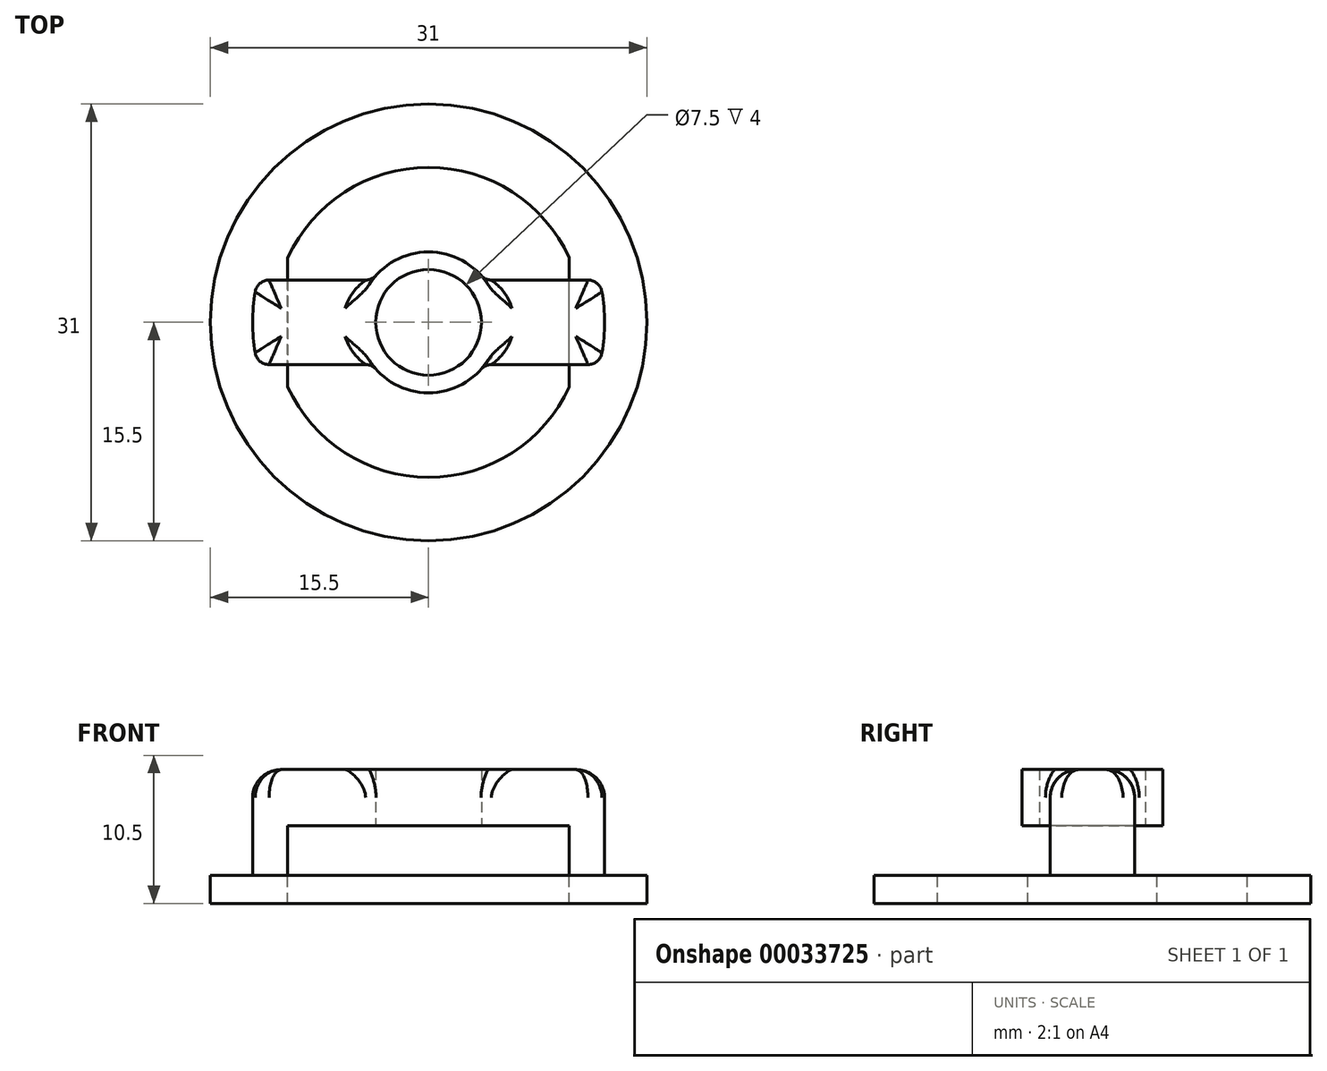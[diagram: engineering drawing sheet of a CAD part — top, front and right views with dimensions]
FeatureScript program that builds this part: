
annotation { "Feature Type Name" : "Feature", "Feature Type Description" : "" }
export const myFeature = defineFeature(function(context is Context, id is Id, definition is map)
    precondition{}
    {
        {
            var Q0;
            Q0=qCreatedBy(makeId("Top.planeOp"),FACE);
            var sketch = newSketch(context, id + "F0", { "sketchPlane" : qUnion([Q0])});
            skCircle(sketch, "E0", {"center": v(0, 0) * mm, "radius": 15.5 * mm});
            skLineSegment(sketch, "E1", {"start": v(-12.13, 3) * mm, "end": v(-10, 3) * mm});
            skLineSegment(sketch, "E2", {"start": v(-12.13, -3) * mm, "end": v(-10, -3) * mm});
            skLineSegment(sketch, "E3", {"start": v(-10, 0) * mm, "end": v(-10, 4.58) * mm});
            skLineSegment(sketch, "E4", {"start": v(-10, 0) * mm, "end": v(-10, -4.58) * mm});
            skLineSegment(sketch, "E5", {"start": v(10, -3) * mm, "end": v(12.13, -3) * mm});
            skLineSegment(sketch, "E6", {"start": v(10, 3) * mm, "end": v(12.13, 3) * mm});
            skLineSegment(sketch, "E7", {"start": v(10, -4.58) * mm, "end": v(10, 4.58) * mm});
            skArc(sketch, "E8", {"start": v(-10, -4.58) * mm, "mid": v(0, -11) * mm, "end": v(10, -4.58) * mm});
            skArc(sketch, "E9", {"start": v(10, 4.58) * mm, "mid": v(0, 11) * mm, "end": v(-10, 4.58) * mm});
            skArc(sketch, "E10", {"start": v(-12.13, 3) * mm, "mid": v(-12.5, 0) * mm, "end": v(-12.13, -3) * mm});
            skArc(sketch, "E11", {"start": v(12.13, -3) * mm, "mid": v(12.5, 0) * mm, "end": v(12.13, 3) * mm});
            skSolve(sketch);
        }
        {
            var Q0;
            Q0=makeQuery(id+"F0.imprint","IMPRINT",FACE,{"disambiguationData":[TD([[makeQuery(id+"F0.imprint","IMPRINT",EDGE,{"derivedFrom":sQuery(id+"F0.wireOp",EDGE,"E0")}),1.0]])]});
            var Q1;
            {var subQ4=sQuery(id+"F0.wireOp",EDGE,"E1");Q1=makeQuery(id+"F0.imprint","IMPRINT",FACE,{"disambiguationData":[TD([[makeQuery(id+"F0.imprint","IMPRINT",EDGE,{"derivedFrom":subQ4}),-1.0]])]});}
            var Q2;
            {var subQ2=sQuery(id+"F0.wireOp",EDGE,"E5");Q2=makeQuery(id+"F0.imprint","IMPRINT",FACE,{"disambiguationData":[TD([[makeQuery(id+"F0.imprint","IMPRINT",EDGE,{"derivedFrom":subQ2}),1.0]])]});}
            extrude(context, id + "F1", {"entities" : qUnion([Q0, Q1, Q2]), "oppositeDirection" : true, "depth" : 2 * mm});
        }
        {
            var Q0;
            {var subQ4=sQuery(id+"F0.wireOp",EDGE,"E1");Q0=makeQuery(id+"F0.imprint","IMPRINT",FACE,{"disambiguationData":[TD([[makeQuery(id+"F0.imprint","IMPRINT",EDGE,{"derivedFrom":subQ4}),-1.0]])]});}
            var Q1;
            {var subQ2=sQuery(id+"F0.wireOp",EDGE,"E5");Q1=makeQuery(id+"F0.imprint","IMPRINT",FACE,{"disambiguationData":[TD([[makeQuery(id+"F0.imprint","IMPRINT",EDGE,{"derivedFrom":subQ2}),1.0]])]});}
            extrude(context, id + "F2", {"entities" : qUnion([Q0, Q1]), "operationType" : NewBodyOperationType.ADD, "depth" : 3.5 * mm});
        }
        {
            var Q0;
            Q0=makeQuery(id+"F2.opExtrude","CAP_FACE",FACE,{"disambiguationData":[OSD([sQuery(id+"F0.wireOp",EDGE,"E1"),sQuery(id+"F0.wireOp",EDGE,"E2"),sQuery(id+"F0.wireOp",EDGE,"E3"),sQuery(id+"F0.wireOp",EDGE,"E4"),sQuery(id+"F0.wireOp",EDGE,"E10")])],"isStart":false});
            var sketch = newSketch(context, id + "F3", { "sketchPlane" : qUnion([Q0])});
            skCircle(sketch, "E12", {"center": v(0, 0) * mm, "radius": 3.75 * mm});
            skCircle(sketch, "E13", {"center": v(0, 0) * mm, "radius": 5 * mm});
            skLineSegment(sketch, "E14", {"start": v(-10, 3) * mm, "end": v(-4, 3) * mm});
            skLineSegment(sketch, "E15", {"start": v(-10, -3) * mm, "end": v(-4, -3) * mm});
            skLineSegment(sketch, "E16.0.0", {"start": v(10, 3) * mm, "end": v(10, -3) * mm});
            skLineSegment(sketch, "E16.0.1", {"start": v(10, -3) * mm, "end": v(12.13, -3) * mm});
            skArc(sketch, "E16.0.2", {"start": v(12.13, -3) * mm, "mid": v(12.5, 0) * mm, "end": v(12.13, 3) * mm});
            skLineSegment(sketch, "E16.0.3", {"start": v(12.13, 3) * mm, "end": v(10, 3) * mm});
            skLineSegment(sketch, "E17", {"start": v(10, 3) * mm, "end": v(4, 3) * mm});
            skLineSegment(sketch, "E18", {"start": v(10, -3) * mm, "end": v(4, -3) * mm});
            skSolve(sketch);
        }
        {
            var Q0;
            Q0 = qSketchRegion(id + "F3", true);
            var Q1;
            {var subQ1=sQuery(id+"F3.wireOp",EDGE,"E14");Q1=makeQuery(id+"F3.imprint","IMPRINT",FACE,{"disambiguationData":[TD([[makeQuery(id+"F3.imprint","IMPRINT",EDGE,{"derivedFrom":subQ1}),-1.0]])]});}
            var Q2;
            Q2=makeQuery(id+"F3.imprint","IMPRINT",FACE,{"disambiguationData":[TD([[makeQuery(id+"F3.imprint","IMPRINT",EDGE,{"derivedFrom":makeQuery(id+"F2.opExtrude","CAP_EDGE",EDGE,{"disambiguationData":[OSD([sQuery(id+"F0.wireOp",EDGE,"E1")])],"isStart":false})}),-1.0]])]});
            extrude(context, id + "F4", {"entities" : qUnion([Q0, Q1, Q2]), "operationType" : NewBodyOperationType.ADD, "depth" : 4 * mm});
        }
        {
            var Q0;
            Q0=makeQuery(id+"F2.opExtrude","CAP_EDGE",EDGE,{"disambiguationData":[OSD([sQuery(id+"F0.wireOp",EDGE,"E2")])],"isStart":true});
            var Q1;
            Q1=makeQuery(id+"F2.opExtrude","CAP_EDGE",EDGE,{"disambiguationData":[OSD([sQuery(id+"F0.wireOp",EDGE,"E1")])],"isStart":true});
            var Q2;
            Q2=makeQuery(id+"F2.opExtrude","CAP_EDGE",EDGE,{"disambiguationData":[OSD([sQuery(id+"F0.wireOp",EDGE,"E5")])],"isStart":true});
            var Q3;
            Q3=makeQuery(id+"F2.opExtrude","CAP_EDGE",EDGE,{"disambiguationData":[OSD([sQuery(id+"F0.wireOp",EDGE,"E6")])],"isStart":true});
            var Q4;
            Q4=makeQuery(id+"F4.opExtrude","CAP_EDGE",EDGE,{"disambiguationData":[OSD([sQuery(id+"F3.wireOp",EDGE,"E16.0.2")])],"isStart":false});
            var Q5;
            Q5=makeQuery(id+"F4.opExtrude","CAP_EDGE",EDGE,{"disambiguationData":[OSD([sQuery(id+"F0.wireOp",EDGE,"E10")])],"isStart":false});
            var Q6;
            Q6=makeQuery(id+"F4.opExtrude","CAP_EDGE",EDGE,{"disambiguationData":[OSD([sQuery(id+"F0.wireOp",EDGE,"E1"),sQuery(id+"F3.wireOp",EDGE,"E14")])],"isStart":false});
            var Q7;
            Q7=makeQuery(id+"F4.opExtrude","CAP_EDGE",EDGE,{"disambiguationData":[OSD([sQuery(id+"F0.wireOp",EDGE,"E2"),sQuery(id+"F3.wireOp",EDGE,"E15")])],"isStart":false});
            var Q8;
            Q8=makeQuery(id+"F4.opExtrude","CAP_EDGE",EDGE,{"disambiguationData":[OSD([sQuery(id+"F3.wireOp",EDGE,"E16.0.3"),sQuery(id+"F3.wireOp",EDGE,"E17")])],"isStart":false});
            var Q9;
            Q9=makeQuery(id+"F4.opExtrude","CAP_EDGE",EDGE,{"disambiguationData":[OSD([sQuery(id+"F3.wireOp",EDGE,"E16.0.1"),sQuery(id+"F3.wireOp",EDGE,"E18")])],"isStart":false});
            fillet(context, id + "F5", {"entities" : qUnion([Q0, Q1, Q2, Q3, Q4, Q5, Q6, Q7, Q8, Q9]), "radius" : 2 * mm, "tangentPropagation" : true, "allowEdgeOverflow" : false});
        }
        {
            var Q0;
            Q0=makeQuery(id+"F2.opExtrude","CAP_EDGE",EDGE,{"disambiguationData":[OSD([sQuery(id+"F0.wireOp",EDGE,"E7")])],"isStart":false});
            var Q1;
            Q1=makeQuery(id+"F2.opExtrude","CAP_EDGE",EDGE,{"disambiguationData":[OSD([sQuery(id+"F0.wireOp",EDGE,"E3"),sQuery(id+"F0.wireOp",EDGE,"E4")])],"isStart":false});
            var Q2;
            Q2=makeQuery(id+"F5.opFillet","BLEND_EDGE",EDGE,{"blendedFrom":[makeQuery(id+"F4.opExtrude","CAP_EDGE",EDGE,{"disambiguationData":[OSD([sQuery(id+"F0.wireOp",EDGE,"E1"),sQuery(id+"F3.wireOp",EDGE,"E14")])],"isStart":false}),makeQuery(id+"F4.opExtrude","CAP_EDGE",EDGE,{"disambiguationData":[OSD([sQuery(id+"F0.wireOp",EDGE,"E10")])],"isStart":false})],"blendedInto":[]});
            var Q3;
            Q3=makeQuery(id+"F5.opFillet","BLEND_EDGE",EDGE,{"blendedFrom":[makeQuery(id+"F4.opExtrude","CAP_EDGE",EDGE,{"disambiguationData":[OSD([sQuery(id+"F0.wireOp",EDGE,"E2"),sQuery(id+"F3.wireOp",EDGE,"E15")])],"isStart":false}),makeQuery(id+"F4.opExtrude","CAP_EDGE",EDGE,{"disambiguationData":[OSD([sQuery(id+"F0.wireOp",EDGE,"E10")])],"isStart":false})],"blendedInto":[]});
            var Q4;
            Q4=makeQuery(id+"F5.opFillet","BLEND_EDGE",EDGE,{"blendedFrom":[makeQuery(id+"F4.opExtrude","CAP_EDGE",EDGE,{"disambiguationData":[OSD([sQuery(id+"F3.wireOp",EDGE,"E16.0.2")])],"isStart":false}),makeQuery(id+"F4.opExtrude","CAP_EDGE",EDGE,{"disambiguationData":[OSD([sQuery(id+"F3.wireOp",EDGE,"E16.0.3"),sQuery(id+"F3.wireOp",EDGE,"E17")])],"isStart":false})],"blendedInto":[]});
            var Q5;
            Q5=makeQuery(id+"F5.opFillet","BLEND_EDGE",EDGE,{"blendedFrom":[makeQuery(id+"F4.opExtrude","CAP_EDGE",EDGE,{"disambiguationData":[OSD([sQuery(id+"F3.wireOp",EDGE,"E16.0.1"),sQuery(id+"F3.wireOp",EDGE,"E18")])],"isStart":false}),makeQuery(id+"F4.opExtrude","CAP_EDGE",EDGE,{"disambiguationData":[OSD([sQuery(id+"F3.wireOp",EDGE,"E16.0.2")])],"isStart":false})],"blendedInto":[]});
            var Q6;
            Q6=makeQuery(id+"F4.opExtrude","SWEPT_EDGE",EDGE,{"disambiguationData":[OSD([sQuery(id+"F3.wireOp",EDGE,"E13"),sQuery(id+"F3.wireOp",EDGE,"E17")])]});
            var Q7;
            Q7=makeQuery(id+"F4.opExtrude","SWEPT_EDGE",EDGE,{"disambiguationData":[OSD([sQuery(id+"F3.wireOp",EDGE,"E13"),sQuery(id+"F3.wireOp",EDGE,"E14")])]});
            var Q8;
            Q8=makeQuery(id+"F4.opExtrude","SWEPT_EDGE",EDGE,{"disambiguationData":[OSD([sQuery(id+"F3.wireOp",EDGE,"E13"),sQuery(id+"F3.wireOp",EDGE,"E15")])]});
            var Q9;
            Q9=makeQuery(id+"F4.opExtrude","SWEPT_EDGE",EDGE,{"disambiguationData":[OSD([sQuery(id+"F3.wireOp",EDGE,"E13"),sQuery(id+"F3.wireOp",EDGE,"E18")])]});
            fillet(context, id + "F6", {"entities" : qUnion([Q0, Q1, Q2, Q3, Q4, Q5, Q6, Q7, Q8, Q9]), "radius" : 1 * mm, "tangentPropagation" : true, "allowEdgeOverflow" : false});
        }
    });
